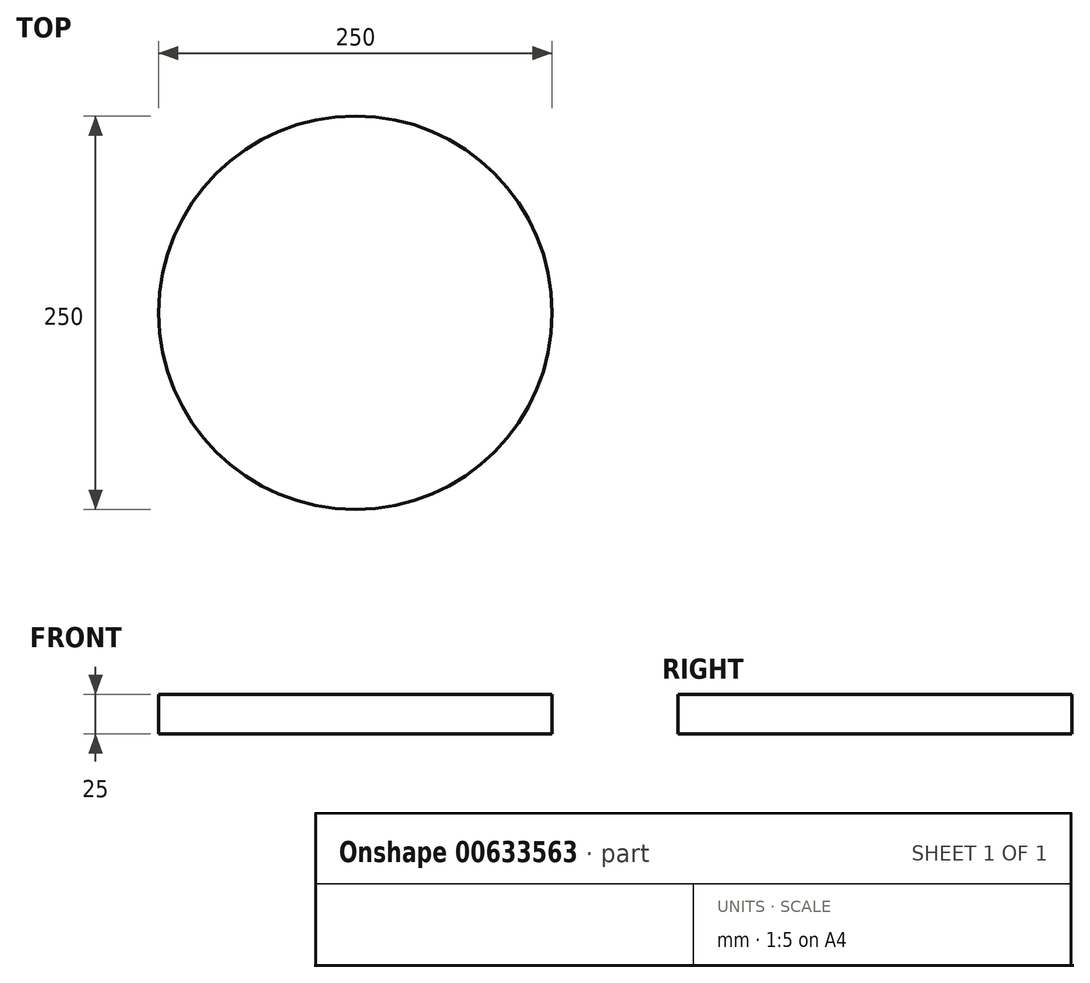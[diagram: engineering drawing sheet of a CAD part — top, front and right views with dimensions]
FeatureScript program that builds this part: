
annotation { "Feature Type Name" : "Feature", "Feature Type Description" : "" }
export const myFeature = defineFeature(function(context is Context, id is Id, definition is map)
    precondition{}
    {
        {
            var Q0;
            Q0=qCreatedBy(makeId("Top.planeOp"),FACE);
            var sketch = newSketch(context, id + "F0", { "sketchPlane" : qUnion([Q0])});
            skCircle(sketch, "E0", {"center": v(0, 0) * mm, "radius": 125 * mm});
            skSolve(sketch);
        }
        {
            var Q0;
            Q0=makeQuery(id+"F0.imprint","IMPRINT",FACE,{"disambiguationData":[TD([[makeQuery(id+"F0.imprint","IMPRINT",EDGE,{"derivedFrom":sQuery(id+"F0.wireOp",EDGE,"E0")}),1.0]])]});
            extrude(context, id + "F1", {"entities" : qUnion([Q0]), "depth" : 25 * mm, "offsetDistance" : 25 * mm});
        }
    });
